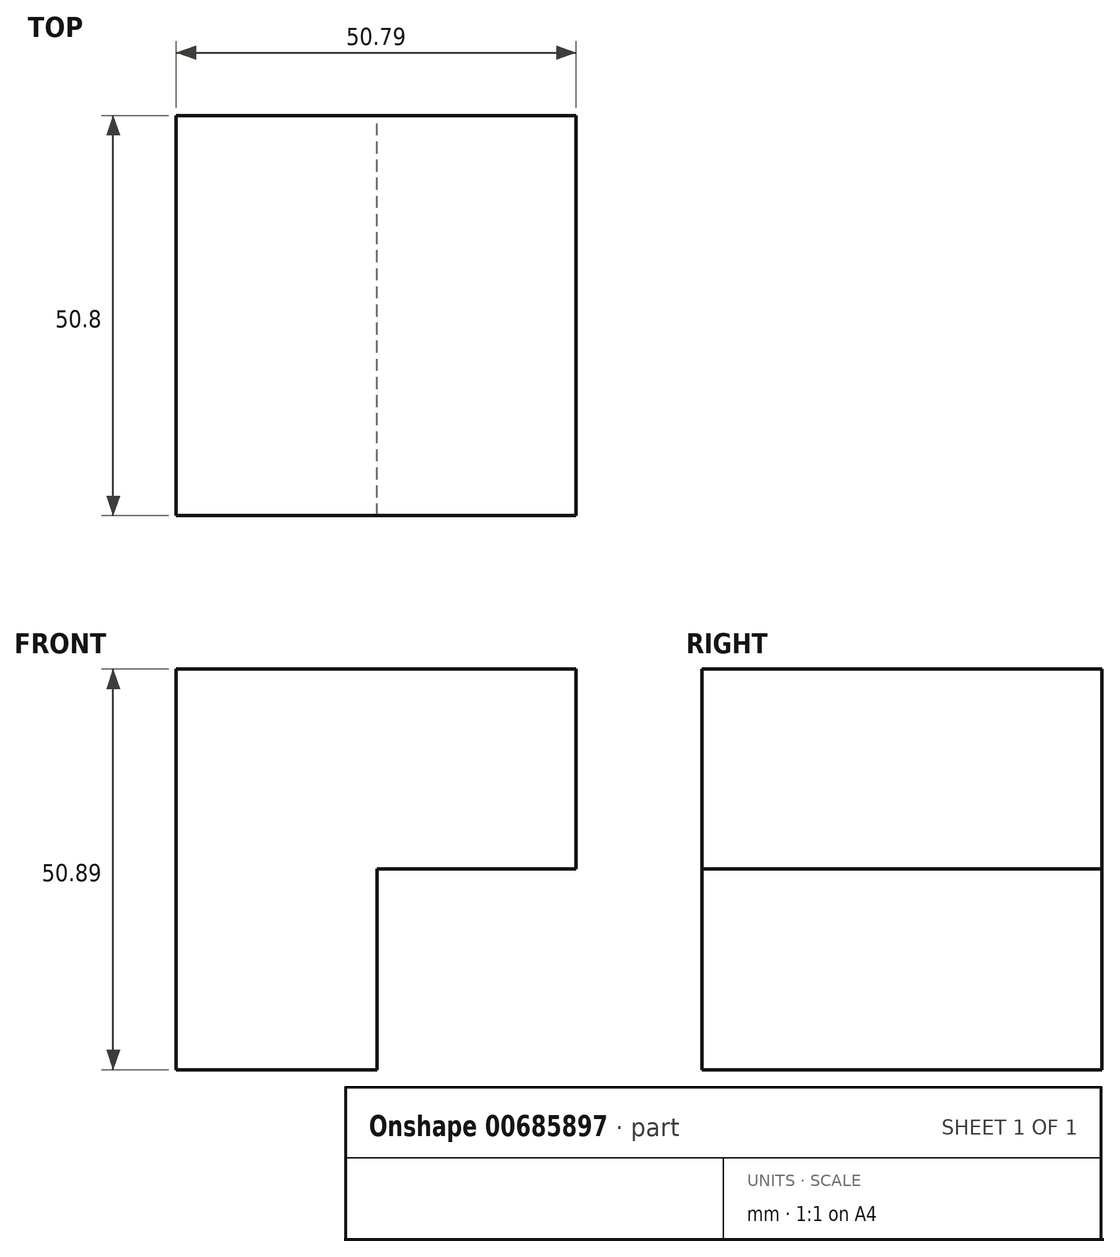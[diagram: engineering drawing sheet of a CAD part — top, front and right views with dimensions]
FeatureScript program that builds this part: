
annotation { "Feature Type Name" : "Feature", "Feature Type Description" : "" }
export const myFeature = defineFeature(function(context is Context, id is Id, definition is map)
    precondition{}
    {
        {
            var Q0;
            Q0=qCreatedBy(makeId("Front.planeOp"),FACE);
            var sketch = newSketch(context, id + "F0", { "sketchPlane" : qUnion([Q0])});
            skLineSegment(sketch, "E0", {"start": v(0, 0) * mm, "end": v(-25.5, 0) * mm});
            skLineSegment(sketch, "E1", {"start": v(-25.5, 0) * mm, "end": v(-25.5, 50.89) * mm});
            skLineSegment(sketch, "E2", {"start": v(-25.5, 50.89) * mm, "end": v(25.3, 50.89) * mm});
            skLineSegment(sketch, "E3", {"start": v(25.3, 50.89) * mm, "end": v(25.3, 25.5) * mm});
            skLineSegment(sketch, "E4", {"start": v(25.3, 25.5) * mm, "end": v(0, 25.5) * mm});
            skLineSegment(sketch, "E5", {"start": v(0, 25.5) * mm, "end": v(0, 0) * mm});
            skSolve(sketch);
        }
        {
            var Q0;
            Q0=makeQuery(id+"F0.imprint","IMPRINT",FACE,{"disambiguationData":[TD([[makeQuery(id+"F0.imprint","IMPRINT",EDGE,{"derivedFrom":sQuery(id+"F0.wireOp",EDGE,"E0")}),-1.0]])]});
            extrude(context, id + "F1", {"entities" : qUnion([Q0]), "depth" : 50.8 * mm, "offsetDistance" : 25.4 * mm});
        }
    });
